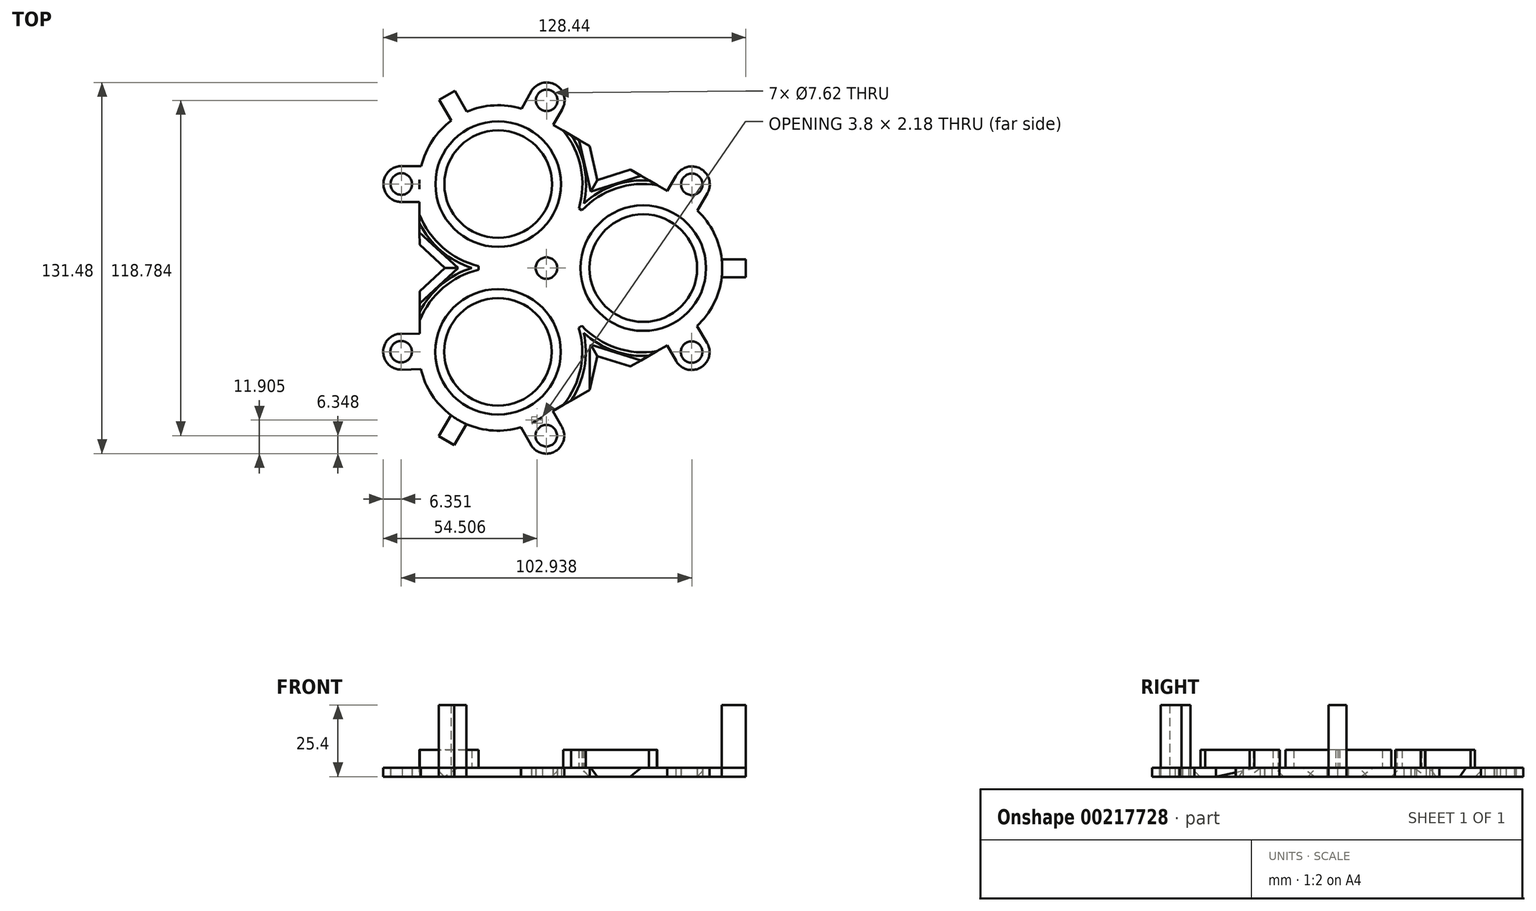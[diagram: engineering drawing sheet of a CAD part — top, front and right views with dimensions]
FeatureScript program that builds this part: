
annotation { "Feature Type Name" : "Feature", "Feature Type Description" : "" }
export const myFeature = defineFeature(function(context is Context, id is Id, definition is map)
    precondition{}
    {
        {
            var Q0;
            Q0=qCreatedBy(makeId("Top.planeOp"),FACE);
            var sketch = newSketch(context, id + "F0", { "sketchPlane" : qUnion([Q0])});
            skCircle(sketch, "E0", {"center": v(0, 0) * mm, "radius": 6.35 * mm});
            skCircle(sketch, "E1", {"center": v(0, 0) * mm, "radius": 3.81 * mm});
            skCircle(sketch, "E2", {"center": v(34.29, -0.04) * mm, "radius": 27.94 * mm});
            skPoint(sketch, "E2.first.point", {"position": v(6.35, 0) * mm});
            skPoint(sketch, "E2.second.point", {"position": v(62.23, 0) * mm});
            skPoint(sketch, "E2.third.point", {"position": v(30, 27.57) * mm});
            skCircle(sketch, "E3.1.1", {"center": v(-17.18, -29.68) * mm, "radius": 27.94 * mm});
            skCircle(sketch, "E3.2.1", {"center": v(-17.11, 29.72) * mm, "radius": 27.94 * mm});
            skLineSegment(sketch, "E3.anchor1", {"start": v(0, 0) * mm, "end": v(34.29, -0.04) * mm, "construction": true});
            skLineSegment(sketch, "E3.anchor2", {"start": v(0, 0) * mm, "end": v(-17.11, 29.72) * mm, "construction": true});
            skLineSegment(sketch, "E4", {"start": v(-3.11, 53.9) * mm, "end": v(15.27, 43.25) * mm});
            skLineSegment(sketch, "E5", {"start": v(-5.21, -54.92) * mm, "end": v(15.32, -43.14) * mm});
            skLineSegment(sketch, "E6", {"start": v(-44.83, -25.7) * mm, "end": v(-44.89, -8.2) * mm});
            skArc(sketch, "E7.1.0", {"start": v(5.56, 56.21) * mm, "mid": v(3.18, 64.92) * mm, "end": v(-5.5, 62.44) * mm});
            skCircle(sketch, "E7.1.1", {"center": v(0.07, 59.4) * mm, "radius": 3.81 * mm});
            skLineSegment(sketch, "E7.1.3", {"start": v(0.07, 59.4) * mm, "end": v(-17.11, 29.72) * mm, "construction": true});
            skPoint(sketch, "E7.1.4", {"position": v(0.07, 59.4) * mm});
            skLineSegment(sketch, "E7.1.5", {"start": v(0.07, 59.4) * mm, "end": v(-17.04, 89.1) * mm, "construction": true});
            skCircle(sketch, "E7.2.1", {"center": v(-51.4, 29.75) * mm, "radius": 3.81 * mm});
            skLineSegment(sketch, "E7.2.3", {"start": v(-51.4, 29.75) * mm, "end": v(-17.11, 29.72) * mm, "construction": true});
            skPoint(sketch, "E7.2.4", {"position": v(-51.4, 29.75) * mm});
            skLineSegment(sketch, "E7.2.5", {"start": v(-51.4, 29.75) * mm, "end": v(-68.58, 0.08) * mm, "construction": true});
            skArc(sketch, "E7.2.7", {"start": v(-51.4, 36.1) * mm, "mid": v(-57.75, 29.6) * mm, "end": v(-51.1, 23.41) * mm});
            skArc(sketch, "E8.1.0", {"start": v(48.23, -24.25) * mm, "mid": v(49.82, -35.9) * mm, "end": v(56.83, -26.46) * mm});
            skCircle(sketch, "E8.1.1", {"center": v(51.4, -29.75) * mm, "radius": 3.81 * mm});
            skArc(sketch, "E8.2.0", {"start": v(56.97, 26.46) * mm, "mid": v(54.5, 35.21) * mm, "end": v(45.82, 32.54) * mm});
            skCircle(sketch, "E8.2.1", {"center": v(51.47, 29.64) * mm, "radius": 3.81 * mm});
            skArc(sketch, "E9.1.0", {"start": v(-45.12, -29.64) * mm, "mid": v(-56, -25.2) * mm, "end": v(-51.33, -35.99) * mm});
            skCircle(sketch, "E9.1.1", {"center": v(-51.47, -29.64) * mm, "radius": 3.81 * mm});
            skArc(sketch, "E9.2.0", {"start": v(-3.24, -53.89) * mm, "mid": v(-1.57, -65.56) * mm, "end": v(5.27, -55.95) * mm});
            skCircle(sketch, "E9.2.1", {"center": v(-0.07, -59.4) * mm, "radius": 3.81 * mm});
            skLineSegment(sketch, "E10", {"start": v(-17.11, 29.72) * mm, "end": v(-35.24, 61.2) * mm});
            skLineSegment(sketch, "E11", {"start": v(-31.05, 53.93) * mm, "end": v(-35.24, 61.2) * mm});
            skLineSegment(sketch, "E12", {"start": v(-35.24, 61.2) * mm, "end": v(-32.48, 62.78) * mm});
            skLineSegment(sketch, "E13", {"start": v(-32.48, 62.78) * mm, "end": v(-28.21, 55.36) * mm});
            skLineSegment(sketch, "E14", {"start": v(-35.24, 61.2) * mm, "end": v(-37.99, 59.6) * mm});
            skLineSegment(sketch, "E15", {"start": v(-37.99, 59.6) * mm, "end": v(-33.71, 52.19) * mm});
            skLineSegment(sketch, "E16.1.0", {"start": v(-38.12, -59.52) * mm, "end": v(-33.83, -52.1) * mm});
            skLineSegment(sketch, "E16.1.1", {"start": v(-17.18, -29.68) * mm, "end": v(-35.38, -61.11) * mm});
            skLineSegment(sketch, "E16.1.2", {"start": v(-35.38, -61.11) * mm, "end": v(-32.63, -62.7) * mm});
            skLineSegment(sketch, "E16.1.3", {"start": v(-32.63, -62.7) * mm, "end": v(-28.34, -55.3) * mm});
            skLineSegment(sketch, "E16.1.4", {"start": v(-35.38, -61.11) * mm, "end": v(-38.12, -59.52) * mm});
            skLineSegment(sketch, "E16.2.0", {"start": v(70.6, -3.26) * mm, "end": v(62.05, -3.25) * mm});
            skLineSegment(sketch, "E16.2.1", {"start": v(34.29, -0.04) * mm, "end": v(70.61, -0.08) * mm});
            skLineSegment(sketch, "E16.2.2", {"start": v(70.61, -0.08) * mm, "end": v(70.62, 3.1) * mm});
            skLineSegment(sketch, "E16.2.3", {"start": v(70.62, 3.1) * mm, "end": v(62.05, 3.1) * mm});
            skLineSegment(sketch, "E16.2.4", {"start": v(70.61, -0.08) * mm, "end": v(70.6, -3.26) * mm});
            skLineSegment(sketch, "E17", {"start": v(-51.71, 23.41) * mm, "end": v(-44.33, 23.41) * mm});
            skLineSegment(sketch, "E18", {"start": v(-51.4, 36.1) * mm, "end": v(-44.31, 36.1) * mm});
            skLineSegment(sketch, "E19", {"start": v(0.07, 59.4) * mm, "end": v(8.54, 54.49) * mm});
            skLineSegment(sketch, "E20", {"start": v(5.56, 56.21) * mm, "end": v(2.4, 50.7) * mm});
            skLineSegment(sketch, "E21", {"start": v(0.07, 59.4) * mm, "end": v(-10.93, 65.76) * mm});
            skLineSegment(sketch, "E22", {"start": v(-5.43, 62.57) * mm, "end": v(-8.82, 56.4) * mm});
            skLineSegment(sketch, "E23.1.0", {"start": v(-51.46, -23.29) * mm, "end": v(-45.11, -23.27) * mm});
            skLineSegment(sketch, "E23.1.1", {"start": v(-51.48, -35.99) * mm, "end": v(-44.43, -35.83) * mm});
            skLineSegment(sketch, "E23.1.2", {"start": v(-5.57, -62.57) * mm, "end": v(-9.11, -56.43) * mm});
            skLineSegment(sketch, "E23.1.3", {"start": v(5.58, -56.49) * mm, "end": v(1.89, -50.1) * mm});
            skLineSegment(sketch, "E23.2.0", {"start": v(45.9, -32.92) * mm, "end": v(42.7, -27.43) * mm});
            skLineSegment(sketch, "E23.2.1", {"start": v(56.9, -26.59) * mm, "end": v(53.25, -20.56) * mm});
            skLineSegment(sketch, "E23.2.2", {"start": v(56.97, 26.46) * mm, "end": v(53.42, 20.32) * mm});
            skLineSegment(sketch, "E23.2.3", {"start": v(46.13, 33.08) * mm, "end": v(42.44, 26.69) * mm});
            skLineSegment(sketch, "E24.trimOffspring", {"start": v(48.29, 24.14) * mm, "end": v(48.29, 24.14) * mm});
            skLineSegment(sketch, "E25", {"start": v(-45.11, -23.27) * mm, "end": v(-44.37, -23.27) * mm});
            skLineSegment(sketch, "E26", {"start": v(42.7, -27.43) * mm, "end": v(42.27, -26.81) * mm});
            skCircle(sketch, "E27", {"center": v(-17.11, 29.72) * mm, "radius": 19.05 * mm});
            skCircle(sketch, "E28", {"center": v(34.29, -0.04) * mm, "radius": 19.05 * mm});
            skCircle(sketch, "E29", {"center": v(-17.18, -29.68) * mm, "radius": 19.05 * mm});
            skLineSegment(sketch, "E30", {"start": v(-44.94, 8.25) * mm, "end": v(-36, 0) * mm});
            skLineSegment(sketch, "E31.MirrorCS", {"start": v(-44.94, -8.25) * mm, "end": v(-36, 0) * mm});
            skLineSegment(sketch, "E32.trimOffspring", {"start": v(-44.94, 8.25) * mm, "end": v(-45, 31.32) * mm});
            skLineSegment(sketch, "E33.1.0", {"start": v(29.61, -34.8) * mm, "end": v(18, -31.18) * mm});
            skLineSegment(sketch, "E33.1.1", {"start": v(15.32, -43.04) * mm, "end": v(18, -31.18) * mm});
            skLineSegment(sketch, "E33.2.0", {"start": v(15.32, 43.04) * mm, "end": v(18, 31.18) * mm});
            skLineSegment(sketch, "E33.2.1", {"start": v(29.61, 34.8) * mm, "end": v(18, 31.18) * mm});
            skLineSegment(sketch, "E34", {"start": v(15.32, 43.04) * mm, "end": v(15.27, 43.25) * mm});
            skLineSegment(sketch, "E35", {"start": v(29.61, 34.8) * mm, "end": v(29.8, 34.84) * mm});
            skLineSegment(sketch, "E36.trimOffspring", {"start": v(29.8, 34.84) * mm, "end": v(48.29, 24.14) * mm});
            skLineSegment(sketch, "E37", {"start": v(29.61, -34.8) * mm, "end": v(29.8, -34.83) * mm});
            skLineSegment(sketch, "E38", {"start": v(15.32, -43.04) * mm, "end": v(15.32, -43.14) * mm});
            skLineSegment(sketch, "E39.trimOffspring", {"start": v(29.8, -34.83) * mm, "end": v(48.2, -24.27) * mm});
            skSolve(sketch);
        }
        {
            var Q0;
            Q0 = qSketchRegion(id + "F0", true);
            var Q1;
            Q1=makeQuery(id+"F0.imprint","IMPRINT",FACE,{"disambiguationData":[TD([[makeQuery(id+"F0.imprint","IMPRINT",EDGE,{"derivedFrom":sQuery(id+"F0.wireOp",EDGE,"E1")}),-1.0]])]});
            extrude(context, id + "F1", {"entities" : qUnion([Q0, Q1]), "depth" : 3.17 * mm});
        }
        {
            var Q0;
            {var subQ0=sQuery(id+"F0.wireOp",EDGE,"E16.2.0");Q0=makeQuery(id+"F0.imprint","IMPRINT",FACE,{"disambiguationData":[TD([[makeQuery(id+"F0.imprint","IMPRINT",EDGE,{"derivedFrom":subQ0}),-1.0]])]});}
            var Q1;
            {var subQ4=sQuery(id+"F0.wireOp",EDGE,"E16.2.2");Q1=makeQuery(id+"F0.imprint","IMPRINT",FACE,{"disambiguationData":[TD([[makeQuery(id+"F0.imprint","IMPRINT",EDGE,{"derivedFrom":subQ4}),1.0]])]});}
            var Q2;
            {var subQ0=sQuery(id+"F0.wireOp",EDGE,"E16.1.0");Q2=makeQuery(id+"F0.imprint","IMPRINT",FACE,{"disambiguationData":[TD([[makeQuery(id+"F0.imprint","IMPRINT",EDGE,{"derivedFrom":subQ0}),-1.0]])]});}
            var Q3;
            {var subQ4=sQuery(id+"F0.wireOp",EDGE,"E16.1.2");Q3=makeQuery(id+"F0.imprint","IMPRINT",FACE,{"disambiguationData":[TD([[makeQuery(id+"F0.imprint","IMPRINT",EDGE,{"derivedFrom":subQ4}),1.0]])]});}
            var Q4;
            {var subQ0=sQuery(id+"F0.wireOp",EDGE,"E11");Q4=makeQuery(id+"F0.imprint","IMPRINT",FACE,{"disambiguationData":[TD([[makeQuery(id+"F0.imprint","IMPRINT",EDGE,{"derivedFrom":subQ0}),-1.0]])]});}
            var Q5;
            {var subQ0=sQuery(id+"F0.wireOp",EDGE,"E11");Q5=makeQuery(id+"F0.imprint","IMPRINT",FACE,{"disambiguationData":[TD([[makeQuery(id+"F0.imprint","IMPRINT",EDGE,{"derivedFrom":subQ0}),1.0]])]});}
            extrude(context, id + "F2", {"entities" : qUnion([Q0, Q1, Q2, Q3, Q4, Q5]), "depth" : 25.4 * mm});
        }
        {
            var Q0;
            Q0=makeQuery(id+"F1.opExtrude","CAP_FACE",FACE,{"disambiguationData":[OSD([sQuery(id+"F0.wireOp",EDGE,"E1"),sQuery(id+"F0.wireOp",EDGE,"E4"),sQuery(id+"F0.wireOp",EDGE,"E5"),sQuery(id+"F0.wireOp",EDGE,"E6"),sQuery(id+"F0.wireOp",EDGE,"E7.1.0"),sQuery(id+"F0.wireOp",EDGE,"E7.1.1"),sQuery(id+"F0.wireOp",EDGE,"E7.2.1"),sQuery(id+"F0.wireOp",EDGE,"E3.2.1"),sQuery(id+"F0.wireOp",EDGE,"E7.2.7"),sQuery(id+"F0.wireOp",EDGE,"E8.1.0"),sQuery(id+"F0.wireOp",EDGE,"E8.1.1"),sQuery(id+"F0.wireOp",EDGE,"E8.2.0"),sQuery(id+"F0.wireOp",EDGE,"E8.2.1"),sQuery(id+"F0.wireOp",EDGE,"E2"),sQuery(id+"F0.wireOp",EDGE,"E9.1.0"),sQuery(id+"F0.wireOp",EDGE,"E9.1.1"),sQuery(id+"F0.wireOp",EDGE,"E9.2.0"),sQuery(id+"F0.wireOp",EDGE,"E9.2.1"),sQuery(id+"F0.wireOp",EDGE,"E3.1.1"),sQuery(id+"F0.wireOp",EDGE,"E12"),sQuery(id+"F0.wireOp",EDGE,"E13"),sQuery(id+"F0.wireOp",EDGE,"E14"),sQuery(id+"F0.wireOp",EDGE,"E15"),sQuery(id+"F0.wireOp",EDGE,"E16.1.0"),sQuery(id+"F0.wireOp",EDGE,"E16.1.2"),sQuery(id+"F0.wireOp",EDGE,"E16.1.3"),sQuery(id+"F0.wireOp",EDGE,"E16.1.4"),sQuery(id+"F0.wireOp",EDGE,"E16.2.0"),sQuery(id+"F0.wireOp",EDGE,"E16.2.2"),sQuery(id+"F0.wireOp",EDGE,"E16.2.3"),sQuery(id+"F0.wireOp",EDGE,"E16.2.4"),sQuery(id+"F0.wireOp",EDGE,"E17"),sQuery(id+"F0.wireOp",EDGE,"E18"),sQuery(id+"F0.wireOp",EDGE,"E20"),sQuery(id+"F0.wireOp",EDGE,"E21"),sQuery(id+"F0.wireOp",EDGE,"E22"),sQuery(id+"F0.wireOp",EDGE,"E23.1.0"),sQuery(id+"F0.wireOp",EDGE,"E23.1.1"),sQuery(id+"F0.wireOp",EDGE,"E23.1.2"),sQuery(id+"F0.wireOp",EDGE,"E23.1.3"),sQuery(id+"F0.wireOp",EDGE,"E23.2.0"),sQuery(id+"F0.wireOp",EDGE,"E23.2.1"),sQuery(id+"F0.wireOp",EDGE,"E23.2.2"),sQuery(id+"F0.wireOp",EDGE,"E23.2.3"),sQuery(id+"F0.wireOp",EDGE,"E25"),sQuery(id+"F0.wireOp",EDGE,"E26")])],"isStart":false});
            var sketch = newSketch(context, id + "F3", { "sketchPlane" : qUnion([Q0])});
            skArc(sketch, "E40", {"start": v(-44.97, 19) * mm, "mid": v(-36.76, 7.25) * mm, "end": v(-24.01, 0.68) * mm});
            skArc(sketch, "E41", {"start": v(39.2, 29.4) * mm, "mid": v(24.78, 28.25) * mm, "end": v(12.6, 20.45) * mm});
            skArc(sketch, "E42", {"start": v(-24.01, -0.62) * mm, "mid": v(-36.61, -7.03) * mm, "end": v(-44.86, -18.5) * mm});
            skArc(sketch, "E43", {"start": v(-26.43, 0.03) * mm, "mid": v(-37.21, -5.87) * mm, "end": v(-44.86, -15.48) * mm});
            skArc(sketch, "E44", {"start": v(13.2, -22.9) * mm, "mid": v(23.92, -29.37) * mm, "end": v(36.32, -31.09) * mm});
            skLineSegment(sketch, "E45", {"start": v(-44.86, -18.5) * mm, "end": v(-44.86, -15.48) * mm});
            skLineSegment(sketch, "E46", {"start": v(5.98, -48.5) * mm, "end": v(8.71, -46.93) * mm});
            skArc(sketch, "E47.trimOffspring", {"start": v(5.98, -48.5) * mm, "mid": v(12.1, -35.5) * mm, "end": v(11.42, -21.13) * mm});
            skArc(sketch, "E48.trimOffspring", {"start": v(8.71, -46.93) * mm, "mid": v(13.4, -35.38) * mm, "end": v(13.2, -22.9) * mm});
            skLineSegment(sketch, "E49", {"start": v(-24.01, -0.62) * mm, "end": v(-24.01, 0.68) * mm});
            skLineSegment(sketch, "E50", {"start": v(11.42, -21.13) * mm, "end": v(12.55, -20.48) * mm});
            skLineSegment(sketch, "E51", {"start": v(36.32, -31.09) * mm, "end": v(39.1, -29.5) * mm});
            skLineSegment(sketch, "E52", {"start": v(39.2, 29.4) * mm, "end": v(36.44, 31) * mm});
            skArc(sketch, "E53.trimOffspring", {"start": v(36.44, 31) * mm, "mid": v(24, 29.33) * mm, "end": v(13.24, 22.88) * mm});
            skArc(sketch, "E54.trimOffspring", {"start": v(12.55, -20.48) * mm, "mid": v(24.7, -28.3) * mm, "end": v(39.1, -29.5) * mm});
            skLineSegment(sketch, "E55", {"start": v(8.74, 47.04) * mm, "end": v(5.97, 48.64) * mm});
            skLineSegment(sketch, "E56", {"start": v(-44.96, 15.84) * mm, "end": v(-44.97, 19) * mm});
            skArc(sketch, "E57.trimOffspring", {"start": v(-44.96, 15.84) * mm, "mid": v(-37.3, 6.05) * mm, "end": v(-26.43, 0.03) * mm});
            skArc(sketch, "E58.trimOffspring", {"start": v(13.24, 22.88) * mm, "mid": v(13.48, 35.42) * mm, "end": v(8.74, 47.04) * mm});
            skLineSegment(sketch, "E59", {"start": v(12.6, 20.45) * mm, "end": v(11.47, 21.1) * mm});
            skArc(sketch, "E60.trimOffspring", {"start": v(11.47, 21.1) * mm, "mid": v(12.16, 35.56) * mm, "end": v(5.97, 48.64) * mm});
            skSolve(sketch);
        }
        {
            var Q0;
            Q0 = qSketchRegion(id + "F3", true);
            extrude(context, id + "F4", {"entities" : qUnion([Q0]), "depth" : 6.35 * mm});
        }
        {
            var Q0;
            Q0=makeQuery(id+"F1.opExtrude","CAP_EDGE",EDGE,{"disambiguationData":[OSD([sQuery(id+"F0.wireOp",EDGE,"E29")])],"isStart":false});
            var Q1;
            Q1=makeQuery(id+"F1.opExtrude","CAP_EDGE",EDGE,{"disambiguationData":[OSD([sQuery(id+"F0.wireOp",EDGE,"E27")])],"isStart":false});
            var Q2;
            Q2=makeQuery(id+"F1.opExtrude","CAP_EDGE",EDGE,{"disambiguationData":[OSD([sQuery(id+"F0.wireOp",EDGE,"E28")])],"isStart":false});
            chamfer(context, id + "F5", {"entities" : qUnion([Q0, Q1, Q2]), "width" : 3.17 * mm, "tangentPropagation" : true});
        }
        {
            var Q0;
            Q0=makeQuery(id+"F1.opExtrude","CAP_EDGE",EDGE,{"disambiguationData":[OSD([sQuery(id+"F0.wireOp",EDGE,"E33.2.0")])],"isStart":false});
            var Q1;
            Q1=makeQuery(id+"F1.opExtrude","CAP_EDGE",EDGE,{"disambiguationData":[OSD([sQuery(id+"F0.wireOp",EDGE,"E33.2.1")])],"isStart":false});
            var Q2;
            Q2=makeQuery(id+"F1.opExtrude","CAP_EDGE",EDGE,{"disambiguationData":[OSD([sQuery(id+"F0.wireOp",EDGE,"E30")])],"isStart":false});
            var Q3;
            Q3=makeQuery(id+"F1.opExtrude","CAP_EDGE",EDGE,{"disambiguationData":[OSD([sQuery(id+"F0.wireOp",EDGE,"E31.MirrorCS")])],"isStart":false});
            var Q4;
            Q4=makeQuery(id+"F1.opExtrude","CAP_EDGE",EDGE,{"disambiguationData":[OSD([sQuery(id+"F0.wireOp",EDGE,"E33.1.0")])],"isStart":false});
            var Q5;
            Q5=makeQuery(id+"F1.opExtrude","CAP_EDGE",EDGE,{"disambiguationData":[OSD([sQuery(id+"F0.wireOp",EDGE,"E33.1.1")])],"isStart":false});
            chamfer(context, id + "F6", {"entities" : qUnion([Q0, Q1, Q2, Q3, Q4, Q5]), "width" : 3.17 * mm, "tangentPropagation" : true});
        }
    });
